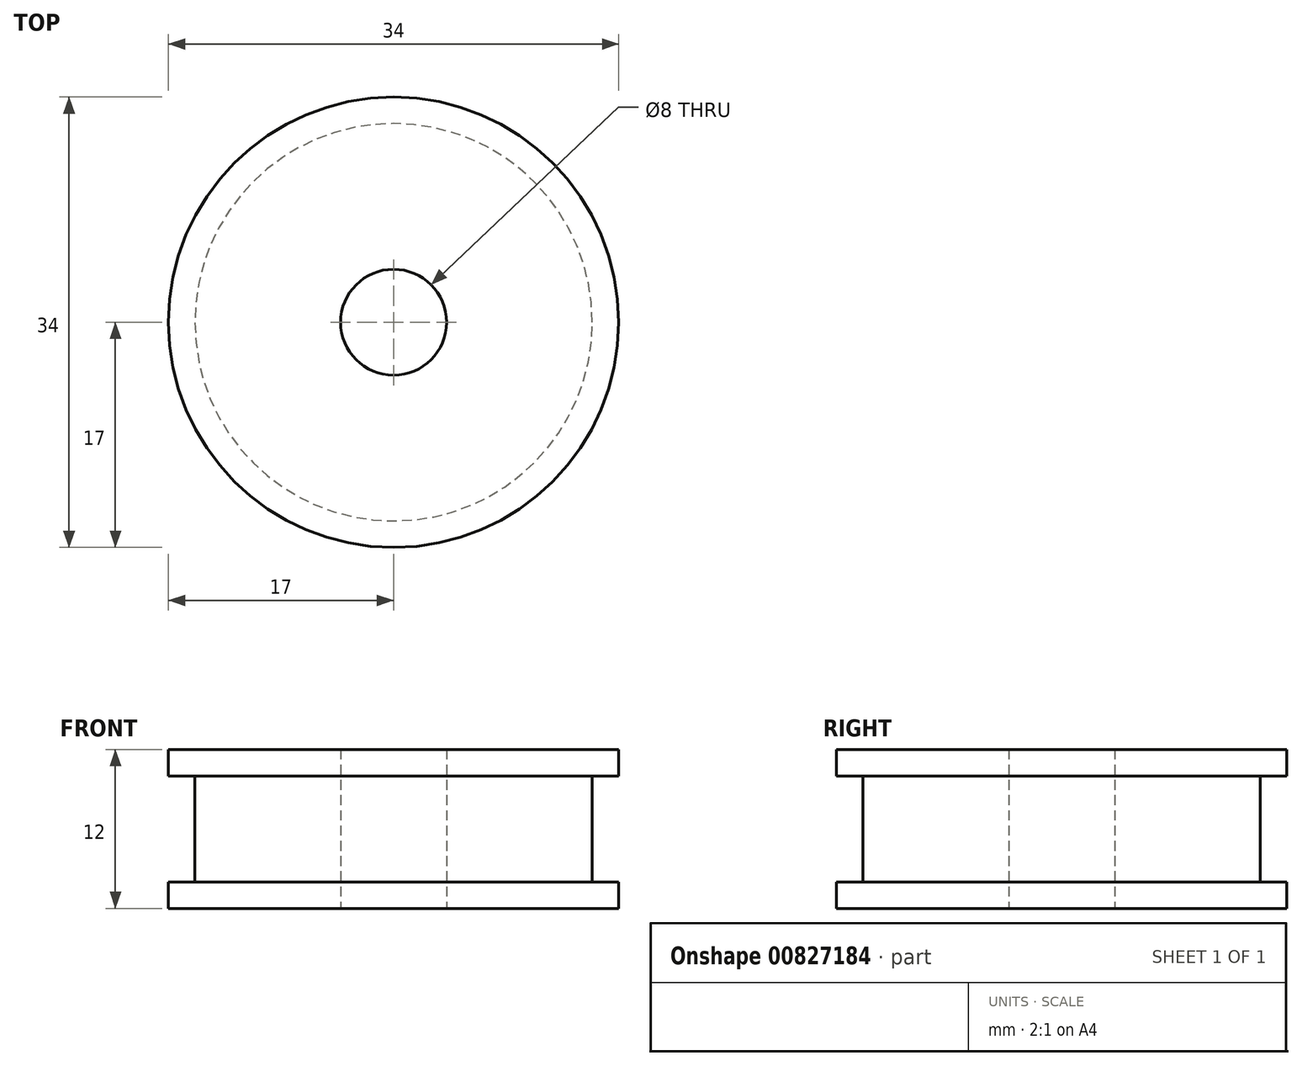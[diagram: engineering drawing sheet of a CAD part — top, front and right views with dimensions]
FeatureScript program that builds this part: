
annotation { "Feature Type Name" : "Feature", "Feature Type Description" : "" }
export const myFeature = defineFeature(function(context is Context, id is Id, definition is map)
    precondition{}
    {
        {
            var Q0;
            Q0=qCreatedBy(makeId("Top.planeOp"),FACE);
            var sketch = newSketch(context, id + "F0", { "sketchPlane" : qUnion([Q0])});
            skCircle(sketch, "E0", {"center": v(0, 0) * mm, "radius": 4 * mm});
            skCircle(sketch, "E1", {"center": v(0, 0) * mm, "radius": 17 * mm});
            skCircle(sketch, "E2", {"center": v(0, 0) * mm, "radius": 15 * mm});
            skSolve(sketch);
        }
        {
            var Q0;
            Q0=makeQuery(id+"F0.imprint","IMPRINT",FACE,{"disambiguationData":[TD([[makeQuery(id+"F0.imprint","IMPRINT",EDGE,{"derivedFrom":sQuery(id+"F0.wireOp",EDGE,"E0")}),-1.0]])]});
            extrude(context, id + "F1", {"entities" : qUnion([Q0]), "depth" : 12 * mm, "offsetDistance" : 25 * mm});
        }
        {
            var Q0;
            Q0=makeQuery(id+"F0.imprint","IMPRINT",FACE,{"disambiguationData":[TD([[makeQuery(id+"F0.imprint","IMPRINT",EDGE,{"derivedFrom":sQuery(id+"F0.wireOp",EDGE,"E1")}),1.0]])]});
            extrude(context, id + "F2", {"entities" : qUnion([Q0]), "operationType" : NewBodyOperationType.ADD, "depth" : 2 * mm, "offsetDistance" : 25 * mm});
        }
        {
            var Q0;
            Q0=makeQuery(id+"F1.opExtrude","CAP_FACE",FACE,{"disambiguationData":[OSD([sQuery(id+"F0.wireOp",EDGE,"E0"),sQuery(id+"F0.wireOp",EDGE,"E2")])],"isStart":false});
            var sketch = newSketch(context, id + "F3", { "sketchPlane" : qUnion([Q0])});
            skCircle(sketch, "E3", {"center": v(0, 0) * mm, "radius": 17 * mm});
            skSolve(sketch);
        }
        {
            var Q0;
            Q0=makeQuery(id+"F3.imprint","IMPRINT",FACE,{"disambiguationData":[TD([[makeQuery(id+"F3.imprint","IMPRINT",EDGE,{"derivedFrom":sQuery(id+"F3.wireOp",EDGE,"E3")}),1.0]])]});
            extrude(context, id + "F4", {"entities" : qUnion([Q0]), "operationType" : NewBodyOperationType.ADD, "oppositeDirection" : true, "depth" : 2 * mm, "offsetDistance" : 25 * mm});
        }
    });
